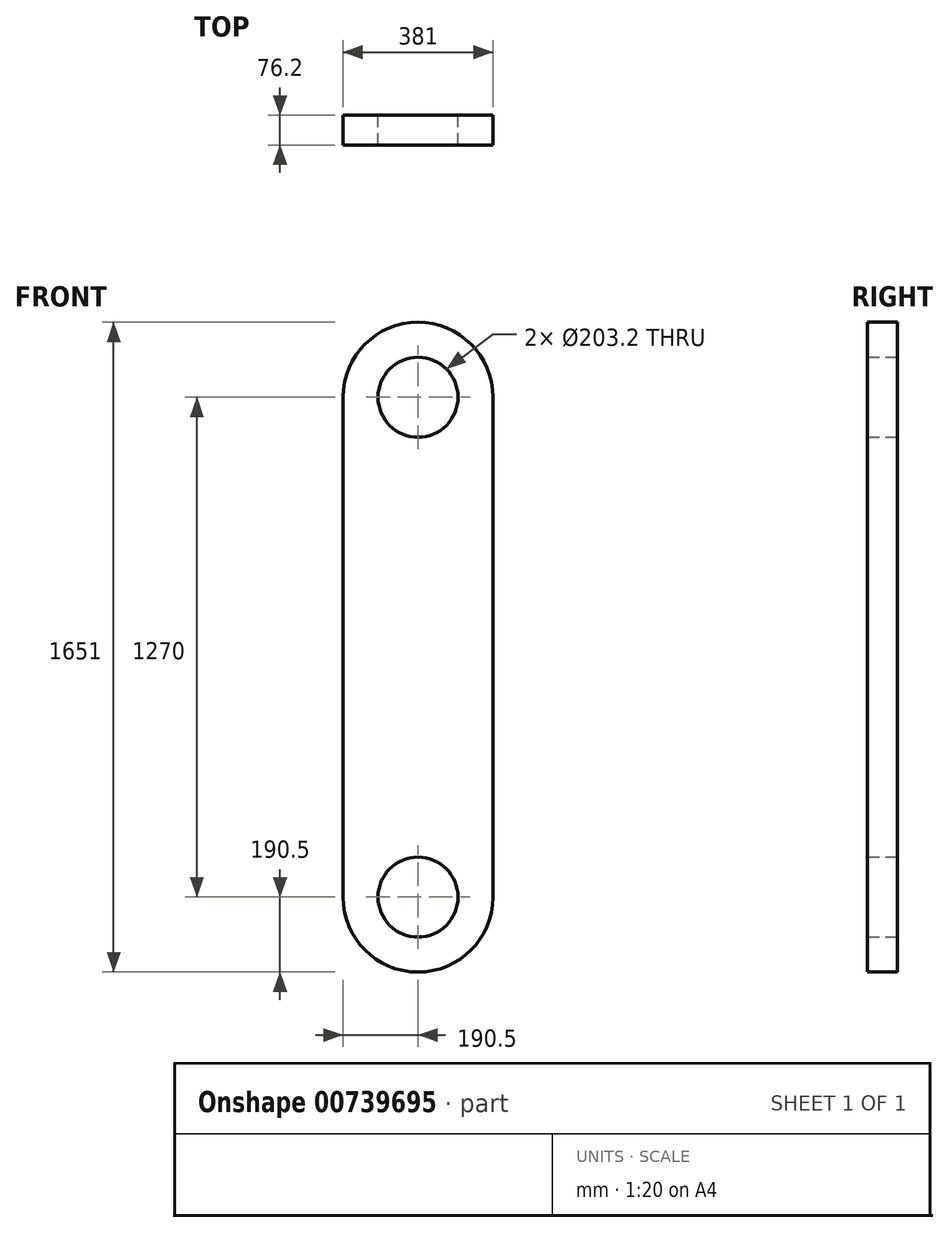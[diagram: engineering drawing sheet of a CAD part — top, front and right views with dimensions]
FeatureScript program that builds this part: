
annotation { "Feature Type Name" : "Feature", "Feature Type Description" : "" }
export const myFeature = defineFeature(function(context is Context, id is Id, definition is map)
    precondition{}
    {
        {
            var Q0;
            Q0=qCreatedBy(makeId("Front.planeOp"),FACE);
            var sketch = newSketch(context, id + "F0", { "sketchPlane" : qUnion([Q0])});
            skLineSegment(sketch, "E0.bottom", {"start": v(190.5, 0) * mm, "end": v(190.5, 0) * mm});
            skLineSegment(sketch, "E0.top", {"start": v(190.5, 1651) * mm, "end": v(190.5, 1651) * mm});
            skLineSegment(sketch, "E0.left", {"start": v(0, 190.5) * mm, "end": v(0, 1460.5) * mm});
            skLineSegment(sketch, "E0.right", {"start": v(381, 190.5) * mm, "end": v(381, 1460.5) * mm});
            skPoint(sketch, "E1.visualSharp", {"position": v(0, 1651) * mm});
            skArc(sketch, "E1.filletArc", {"start": v(190.5, 1651) * mm, "mid": v(55.8, 1595.2) * mm, "end": v(0, 1460.5) * mm});
            skPoint(sketch, "E2.visualSharp", {"position": v(0, 0) * mm});
            skArc(sketch, "E2.filletArc", {"start": v(0, 190.5) * mm, "mid": v(55.8, 55.8) * mm, "end": v(190.5, 0) * mm});
            skPoint(sketch, "E3.visualSharp", {"position": v(381, 0) * mm});
            skArc(sketch, "E3.filletArc", {"start": v(190.5, 0) * mm, "mid": v(325.2, 55.8) * mm, "end": v(381, 190.5) * mm});
            skPoint(sketch, "E4.visualSharp", {"position": v(381, 1651) * mm});
            skArc(sketch, "E4.filletArc", {"start": v(381, 1460.5) * mm, "mid": v(325.2, 1595.2) * mm, "end": v(190.5, 1651) * mm});
            skCircle(sketch, "E5", {"center": v(190.5, 1460.5) * mm, "radius": 101.6 * mm});
            skCircle(sketch, "E6", {"center": v(190.5, 190.5) * mm, "radius": 101.6 * mm});
            skSolve(sketch);
        }
        {
            var Q0;
            Q0=makeQuery(id+"F0.imprint","IMPRINT",FACE,{"disambiguationData":[TD([[makeQuery(id+"F0.imprint","IMPRINT",EDGE,{"derivedFrom":sQuery(id+"F0.wireOp",EDGE,"E0.left")}),-1.0]])]});
            extrude(context, id + "F1", {"entities" : qUnion([Q0]), "depth" : 76.2 * mm, "offsetDistance" : 25.4 * mm});
        }
    });
